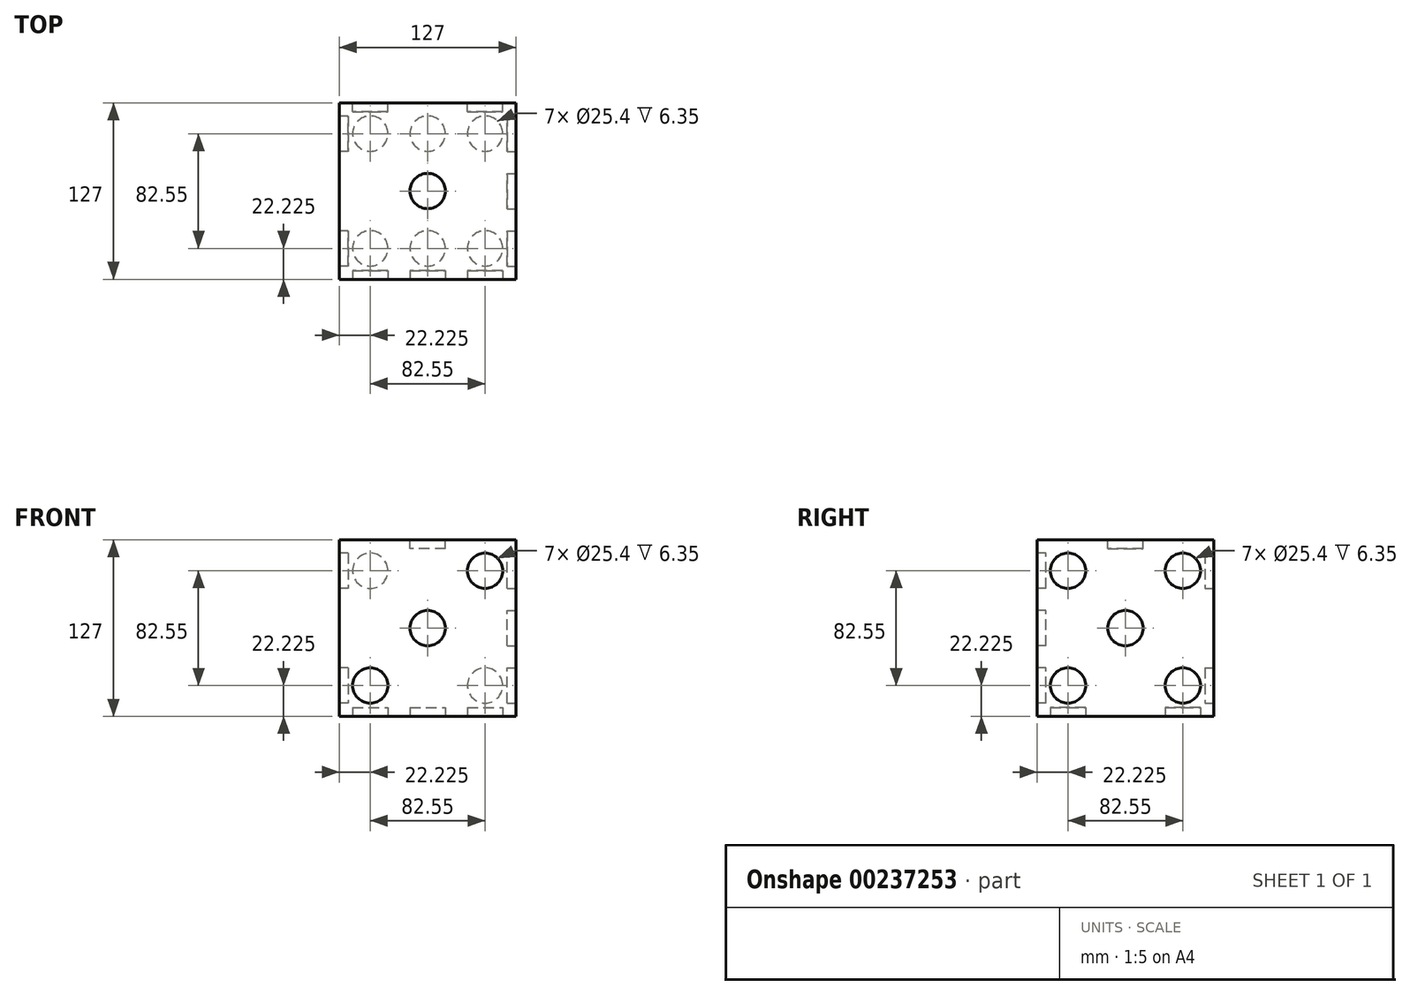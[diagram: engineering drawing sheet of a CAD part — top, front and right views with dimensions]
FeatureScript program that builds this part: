
annotation { "Feature Type Name" : "Feature", "Feature Type Description" : "" }
export const myFeature = defineFeature(function(context is Context, id is Id, definition is map)
    precondition{}
    {
        {
            var Q0;
            Q0=qCreatedBy(makeId("Top.planeOp"),FACE);
            var sketch = newSketch(context, id + "F0", { "sketchPlane" : qUnion([Q0])});
            skLineSegment(sketch, "E0.bottom", {"start": v(0, 0) * mm, "end": v(127, 0) * mm});
            skLineSegment(sketch, "E0.top", {"start": v(0, 127) * mm, "end": v(127, 127) * mm});
            skLineSegment(sketch, "E0.left", {"start": v(0, 0) * mm, "end": v(0, 127) * mm});
            skLineSegment(sketch, "E0.right", {"start": v(127, 0) * mm, "end": v(127, 127) * mm});
            skSolve(sketch);
        }
        {
            var Q0;
            Q0=makeQuery(id+"F0.imprint","IMPRINT",FACE,{"disambiguationData":[TD([[makeQuery(id+"F0.imprint","IMPRINT",EDGE,{"derivedFrom":sQuery(id+"F0.wireOp",EDGE,"E0.bottom")}),1.0]])]});
            extrude(context, id + "F1", {"entities" : qUnion([Q0]), "depth" : 127 * mm});
        }
        {
            var Q0;
            Q0=makeQuery(id+"F1.opExtrude","CAP_FACE",FACE,{"disambiguationData":[OSD([sQuery(id+"F0.wireOp",EDGE,"E0.bottom"),sQuery(id+"F0.wireOp",EDGE,"E0.top"),sQuery(id+"F0.wireOp",EDGE,"E0.left"),sQuery(id+"F0.wireOp",EDGE,"E0.right")])],"isStart":false});
            var sketch = newSketch(context, id + "F2", { "sketchPlane" : qUnion([Q0])});
            skCircle(sketch, "E1", {"center": v(63.5, 63.5) * mm, "radius": 12.7 * mm});
            skSolve(sketch);
        }
        {
            var Q0;
            Q0=makeQuery(id+"F2.imprint","IMPRINT",FACE,{"disambiguationData":[TD([[makeQuery(id+"F2.imprint","IMPRINT",EDGE,{"derivedFrom":sQuery(id+"F2.wireOp",EDGE,"E1")}),1.0]])]});
            extrude(context, id + "F3", {"entities" : qUnion([Q0]), "operationType" : NewBodyOperationType.REMOVE, "oppositeDirection" : true, "depth" : 6.35 * mm});
        }
        {
            var Q0;
            Q0=makeQuery(id+"F1.opExtrude","SWEPT_FACE",FACE,{"disambiguationData":[OSD([sQuery(id+"F0.wireOp",EDGE,"E0.left")])]});
            var sketch = newSketch(context, id + "F4", { "sketchPlane" : qUnion([Q0])});
            skCircle(sketch, "E2", {"center": v(-104.78, 22.22) * mm, "radius": 12.7 * mm});
            skCircle(sketch, "E3", {"center": v(-22.23, 104.78) * mm, "radius": 12.7 * mm});
            skSolve(sketch);
        }
        {
            var Q0;
            Q0=makeQuery(id+"F4.imprint","IMPRINT",FACE,{"disambiguationData":[TD([[makeQuery(id+"F4.imprint","IMPRINT",EDGE,{"derivedFrom":sQuery(id+"F4.wireOp",EDGE,"E2")}),1.0]])]});
            var Q1;
            Q1=makeQuery(id+"F4.imprint","IMPRINT",FACE,{"disambiguationData":[TD([[makeQuery(id+"F4.imprint","IMPRINT",EDGE,{"derivedFrom":sQuery(id+"F4.wireOp",EDGE,"E3")}),1.0]])]});
            extrude(context, id + "F5", {"entities" : qUnion([Q0, Q1]), "operationType" : NewBodyOperationType.REMOVE, "oppositeDirection" : true, "depth" : 6.35 * mm});
        }
        {
            var Q0;
            Q0=makeQuery(id+"F1.opExtrude","SWEPT_FACE",FACE,{"disambiguationData":[OSD([sQuery(id+"F0.wireOp",EDGE,"E0.bottom")])]});
            var sketch = newSketch(context, id + "F6", { "sketchPlane" : qUnion([Q0])});
            skLineSegment(sketch, "E4", {"start": v(0, 0) * mm, "end": v(127, 127) * mm, "construction": true});
            skCircle(sketch, "E5", {"center": v(63.5, 63.5) * mm, "radius": 12.7 * mm});
            skCircle(sketch, "E6", {"center": v(22.23, 22.23) * mm, "radius": 12.7 * mm});
            skCircle(sketch, "E7", {"center": v(104.78, 104.78) * mm, "radius": 12.7 * mm});
            skSolve(sketch);
        }
        {
            var Q0;
            Q0=makeQuery(id+"F6.imprint","IMPRINT",FACE,{"disambiguationData":[TD([[makeQuery(id+"F6.imprint","IMPRINT",EDGE,{"derivedFrom":sQuery(id+"F6.wireOp",EDGE,"E6")}),1.0]])]});
            var Q1;
            Q1=makeQuery(id+"F6.imprint","IMPRINT",FACE,{"disambiguationData":[TD([[makeQuery(id+"F6.imprint","IMPRINT",EDGE,{"derivedFrom":sQuery(id+"F6.wireOp",EDGE,"E5")}),1.0]])]});
            var Q2;
            Q2=makeQuery(id+"F6.imprint","IMPRINT",FACE,{"disambiguationData":[TD([[makeQuery(id+"F6.imprint","IMPRINT",EDGE,{"derivedFrom":sQuery(id+"F6.wireOp",EDGE,"E7")}),1.0]])]});
            extrude(context, id + "F7", {"entities" : qUnion([Q0, Q1, Q2]), "operationType" : NewBodyOperationType.REMOVE, "oppositeDirection" : true, "depth" : 6.35 * mm});
        }
        {
            var Q0;
            Q0=makeQuery(id+"F1.opExtrude","SWEPT_FACE",FACE,{"disambiguationData":[OSD([sQuery(id+"F0.wireOp",EDGE,"E0.top")])]});
            var sketch = newSketch(context, id + "F8", { "sketchPlane" : qUnion([Q0])});
            skCircle(sketch, "E8", {"center": v(-104.77, 104.78) * mm, "radius": 12.7 * mm});
            skCircle(sketch, "E9", {"center": v(-104.77, 22.22) * mm, "radius": 12.7 * mm});
            skCircle(sketch, "E10", {"center": v(-22.23, 22.22) * mm, "radius": 12.7 * mm});
            skCircle(sketch, "E11", {"center": v(-22.23, 104.78) * mm, "radius": 12.7 * mm});
            skSolve(sketch);
        }
        {
            var Q0;
            Q0 = qSketchRegion(id + "F8", true);
            extrude(context, id + "F9", {"entities" : qUnion([Q0]), "operationType" : NewBodyOperationType.REMOVE, "oppositeDirection" : true, "depth" : 6.35 * mm});
        }
        {
            var Q0;
            Q0=makeQuery(id+"F1.opExtrude","SWEPT_FACE",FACE,{"disambiguationData":[OSD([sQuery(id+"F0.wireOp",EDGE,"E0.right")])]});
            var sketch = newSketch(context, id + "F10", { "sketchPlane" : qUnion([Q0])});
            skCircle(sketch, "E12", {"center": v(63.5, 63.5) * mm, "radius": 12.7 * mm});
            skCircle(sketch, "E13", {"center": v(104.77, 104.78) * mm, "radius": 12.7 * mm});
            skCircle(sketch, "E14", {"center": v(22.22, 22.23) * mm, "radius": 12.7 * mm});
            skCircle(sketch, "E15", {"center": v(22.22, 104.78) * mm, "radius": 12.7 * mm});
            skCircle(sketch, "E16", {"center": v(104.77, 22.23) * mm, "radius": 12.7 * mm});
            skSolve(sketch);
        }
        {
            var Q0;
            Q0 = qSketchRegion(id + "F10", true);
            extrude(context, id + "F11", {"entities" : qUnion([Q0]), "operationType" : NewBodyOperationType.REMOVE, "oppositeDirection" : true, "depth" : 6.35 * mm});
        }
        {
            var Q0;
            Q0=makeQuery(id+"F1.opExtrude","CAP_FACE",FACE,{"disambiguationData":[OSD([sQuery(id+"F0.wireOp",EDGE,"E0.bottom"),sQuery(id+"F0.wireOp",EDGE,"E0.top"),sQuery(id+"F0.wireOp",EDGE,"E0.left"),sQuery(id+"F0.wireOp",EDGE,"E0.right")])],"isStart":true});
            var sketch = newSketch(context, id + "F12", { "sketchPlane" : qUnion([Q0])});
            skCircle(sketch, "E17", {"center": v(63.5, -104.78) * mm, "radius": 12.7 * mm});
            skCircle(sketch, "E18", {"center": v(22.23, -104.78) * mm, "radius": 12.7 * mm});
            skCircle(sketch, "E19", {"center": v(104.77, -104.78) * mm, "radius": 12.7 * mm});
            skCircle(sketch, "E20", {"center": v(104.78, -22.23) * mm, "radius": 12.7 * mm});
            skCircle(sketch, "E21", {"center": v(63.5, -22.23) * mm, "radius": 12.7 * mm});
            skCircle(sketch, "E22", {"center": v(22.23, -22.23) * mm, "radius": 12.7 * mm});
            skSolve(sketch);
        }
        {
            var Q0;
            Q0 = qSketchRegion(id + "F12", true);
            extrude(context, id + "F13", {"entities" : qUnion([Q0]), "operationType" : NewBodyOperationType.REMOVE, "oppositeDirection" : true, "depth" : 6.35 * mm});
        }
    });
